# Revit family: KEUCO_59553010002
name_source: partatom
category: Allgemeines Modell
revit_build: Autodesk Revit 2016 (Build: 20150220_1215(x64)
units: mm (PartAtom-declared; Revit-internal decimal feet)

## family parameters
Arbeitsebenenbasiert = Ja
Beim Laden mit Abzugskörper schneiden = Nein
Bemaßung runder Anschluss = Durchmesser verwenden
Gemeinsam genutzt = Nein
Immer vertikal = Nein
Kann Basisbauteil für Bewehrung sein = Nein
Raumberechnungspunkt = Nein
Teiletyp = Normal

## types (1)
- 59553010002
    Artikelnummer = 59553010002
    Ausschreibungstext = KEUCO IXMO Thermostatarmatur UP DN15, 59553010002
hochglanzverchromte Thermostatarmatur 
für Dusche und Wanne aus entzinkungsarmen Messing ,
mit eckiger Rosette, frei positionierbar, 
mit eingebauter Vorrichtung für vertauschte Wasserwege,
integrierter Einbautiefenausgleich von 80 - 110 mm,
hochwertige Temperaturregeleinheit, Sicherheitssperre bei 38°, 
Fertigset bestehend aus:
Griff, Hülse, Rosette (eckig),
Rosette 90 x  90 mm, Stärke 10mm,
Gesamtausladung 80 mm,
passend für UP Funktionseinheit Art.–Nr.59553000070
    Beschreibung = Fertigset bestehend aus:
Griff, Hülse und Rosette (eckig)
passend für UP Funktionseinheit Art.-Nr. 59553 000070
    Breite = 45 mm  [stored 0.147638 ft]
    Gewicht = 0
    Hersteller = KEUCO
    Material = Stahl, verchromt
    Serie = Plan
    URL = https://www.keuco.com
    Verwendung = DU / WA
    Vorgabe-Ansicht = 1219 mm

note: [stored X ft] marks values corroborated as IEEE doubles in the binary element streams (Revit-internal decimal feet)

## geometry (parser evidence)
native form markers: Sweep x3
no freeform markers — native parametric forms only
